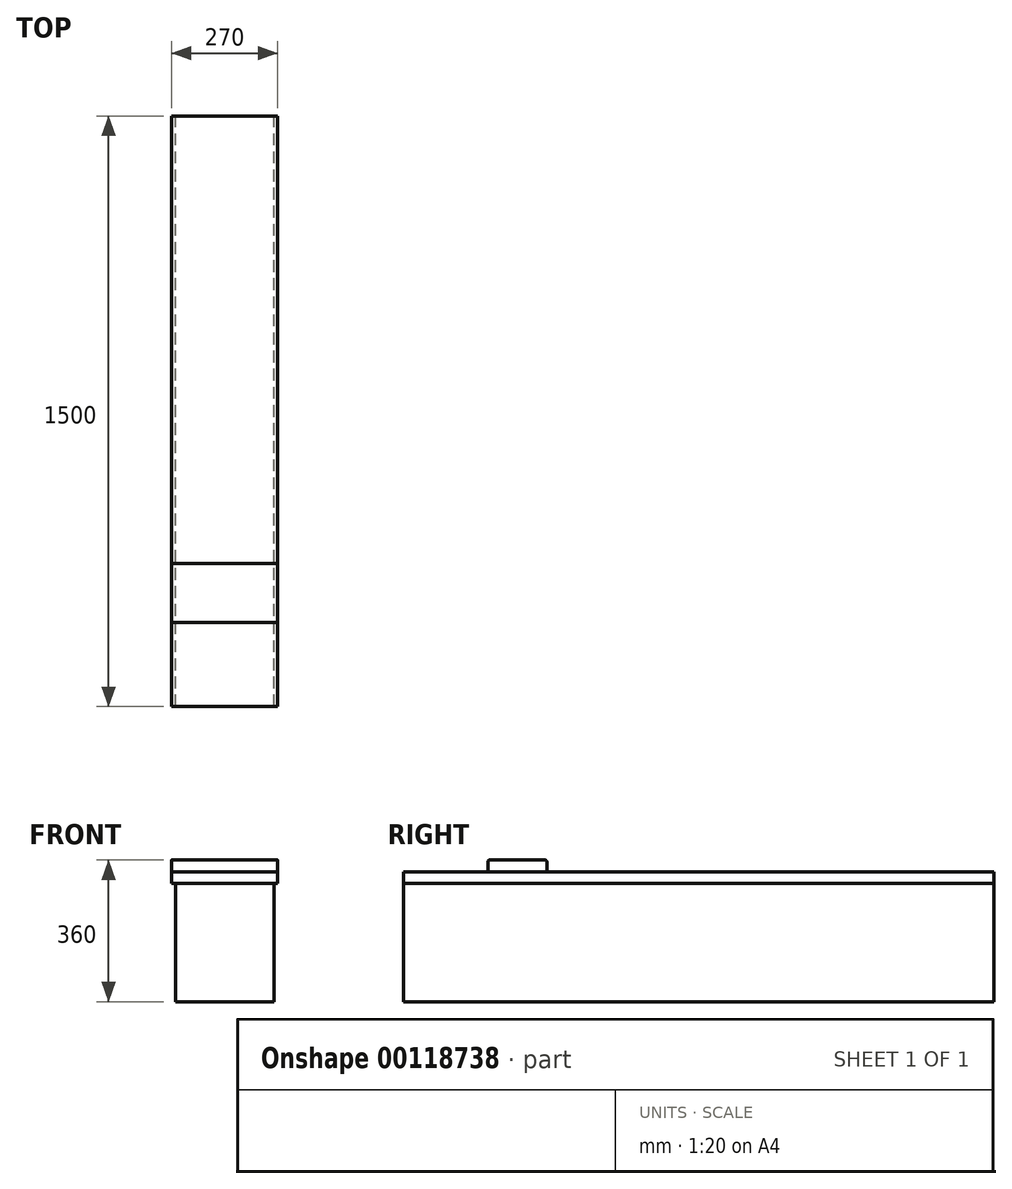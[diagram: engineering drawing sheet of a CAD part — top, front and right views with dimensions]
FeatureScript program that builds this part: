
annotation { "Feature Type Name" : "Feature", "Feature Type Description" : "" }
export const myFeature = defineFeature(function(context is Context, id is Id, definition is map)
    precondition{}
    {
        {
            var Q0;
            Q0=qCreatedBy(makeId("Right.planeOp"),FACE);
            var sketch = newSketch(context, id + "F0", { "sketchPlane" : qUnion([Q0])});
            skLineSegment(sketch, "E0.bottom", {"start": v(-779.82, 194.68) * mm, "end": v(720.18, 194.68) * mm});
            skLineSegment(sketch, "E0.top", {"start": v(-779.82, -105.32) * mm, "end": v(720.18, -105.32) * mm});
            skLineSegment(sketch, "E0.left", {"start": v(-779.82, 194.68) * mm, "end": v(-779.82, -105.32) * mm});
            skLineSegment(sketch, "E0.right", {"start": v(720.18, 194.68) * mm, "end": v(720.18, -105.32) * mm});
            skLineSegment(sketch, "E1.top", {"start": v(-779.82, 224.68) * mm, "end": v(720.18, 224.68) * mm});
            skLineSegment(sketch, "E1.left", {"start": v(-779.82, 194.68) * mm, "end": v(-779.82, 224.68) * mm});
            skLineSegment(sketch, "E1.right", {"start": v(720.18, 194.68) * mm, "end": v(720.18, 224.68) * mm});
            skLineSegment(sketch, "E2.bottom", {"start": v(433.8, 224.68) * mm, "end": v(583.8, 224.68) * mm});
            skLineSegment(sketch, "E2.top", {"start": v(438.8, 254.68) * mm, "end": v(578.8, 254.68) * mm});
            skLineSegment(sketch, "E2.left", {"start": v(433.8, 224.68) * mm, "end": v(433.8, 249.68) * mm});
            skLineSegment(sketch, "E2.right", {"start": v(583.8, 224.68) * mm, "end": v(583.8, 249.68) * mm});
            skLineSegment(sketch, "E3.direction1", {"start": v(433.8, 224.68) * mm, "end": v(-566.2, 224.68) * mm, "construction": true});
            skLineSegment(sketch, "E4.0.1.0", {"start": v(-561.2, 254.68) * mm, "end": v(-421.2, 254.68) * mm});
            skLineSegment(sketch, "E4.3.1.0", {"start": v(-566.2, 224.68) * mm, "end": v(-416.2, 224.68) * mm});
            skLineSegment(sketch, "E4.6.1.0", {"start": v(-416.2, 224.68) * mm, "end": v(-416.2, 249.68) * mm});
            skLineSegment(sketch, "E4.9.1.0", {"start": v(-566.2, 224.68) * mm, "end": v(-566.2, 249.68) * mm});
            skPoint(sketch, "E5.visualSharp", {"position": v(583.8, 254.68) * mm});
            skArc(sketch, "E5.filletArc", {"start": v(583.8, 249.68) * mm, "mid": v(582.34, 253.21) * mm, "end": v(578.8, 254.68) * mm});
            skPoint(sketch, "E6.visualSharp", {"position": v(433.8, 254.68) * mm});
            skArc(sketch, "E6.filletArc", {"start": v(438.8, 254.68) * mm, "mid": v(435.27, 253.21) * mm, "end": v(433.8, 249.68) * mm});
            skPoint(sketch, "E7.visualSharp", {"position": v(-566.2, 254.68) * mm});
            skArc(sketch, "E7.filletArc", {"start": v(-561.2, 254.68) * mm, "mid": v(-564.73, 253.21) * mm, "end": v(-566.2, 249.68) * mm});
            skPoint(sketch, "E8.visualSharp", {"position": v(-416.2, 254.68) * mm});
            skArc(sketch, "E8.filletArc", {"start": v(-416.2, 249.68) * mm, "mid": v(-417.66, 253.21) * mm, "end": v(-421.2, 254.68) * mm});
            skSolve(sketch);
        }
        {
            var Q0;
            Q0=makeQuery(id+"F0.imprint","IMPRINT",FACE,{"disambiguationData":[TD([[makeQuery(id+"F0.imprint","IMPRINT",EDGE,{"derivedFrom":sQuery(id+"F0.wireOp",EDGE,"E0.top")}),1.0]])]});
            extrude(context, id + "F1", {"entities" : qUnion([Q0]), "depth" : 250 * mm});
        }
        {
            var Q0;
            Q0=makeQuery(id+"F0.imprint","IMPRINT",FACE,{"disambiguationData":[TD([[makeQuery(id+"F0.imprint","IMPRINT",EDGE,{"derivedFrom":sQuery(id+"F0.wireOp",EDGE,"E0.bottom")}),1.0]])]});
            extrude(context, id + "F2", {"entities" : qUnion([Q0]), "depth" : 260 * mm, "hasSecondDirection" : true, "secondDirectionOppositeDirection" : true, "secondDirectionDepth" : 10 * mm});
        }
        {
            var Q0;
            Q0=makeQuery(id+"F0.imprint","IMPRINT",FACE,{"disambiguationData":[TD([[makeQuery(id+"F0.imprint","IMPRINT",EDGE,{"derivedFrom":sQuery(id+"F0.wireOp",EDGE,"E4.0.1.0")}),-1.0]])]});
            var Q1;
            Q1=makeQuery(id+"F0.imprint","IMPRINT",FACE,{"disambiguationData":[TD([[makeQuery(id+"F0.imprint","IMPRINT",EDGE,{"derivedFrom":sQuery(id+"F0.wireOp",EDGE,"E2.bottom")}),1.0]])]});
            extrude(context, id + "F3", {"entities" : qUnion([Q0, Q1]), "depth" : 260 * mm, "hasSecondDirection" : true, "secondDirectionOppositeDirection" : true, "secondDirectionDepth" : 10 * mm});
        }
    });
